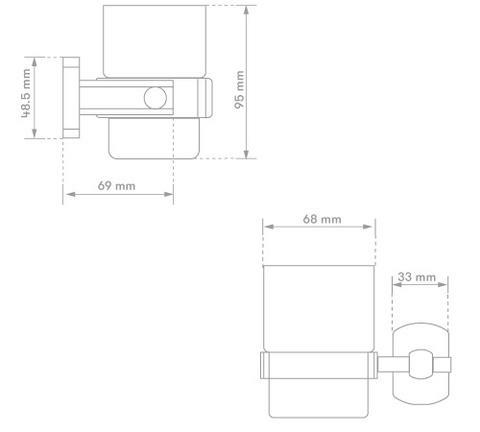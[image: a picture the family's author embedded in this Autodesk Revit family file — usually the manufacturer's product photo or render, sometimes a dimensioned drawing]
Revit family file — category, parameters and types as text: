
# Revit family: BL-2502-11 GANCHO CONTEMPRA
name_source: partatom
category: Plumbing Fixtures
revit_build: Autodesk Revit 2018 (Build: 20170223_1515(x64)
units: mm (PartAtom-declared; Revit-internal decimal feet)

## family parameters
Cut with Voids When Loaded = No
Host = Face
OmniClass Number = 23.31.11.00
Part Type = Normal
Room Calculation Point = No
Round Connector Dimension = Use Diameter
Shared = No

## types (1)
- BL-2502-11
    Alto = 70 mm  [stored 0.229659 ft]
    CW Connection = Yes
    Default Elevation = 0 mm  [stored 0 ft]
    Description = Gancho
    Diametro base = 50 mm  [stored 0.164042 ft]
    HW Connection = Yes
    Link Ficha Tecnica = http://infotecnica.gricol.com
    Manufacturer = Gricol
    Model = BL-2502-11
    Plastico ABS cromado = Plastico - ABS Cromado
    Product Name = GANCHO CONTEMPRA
    Type Image = GANCHO CONTEMPRA.jpg
    URL = https://www.gricol.com
    Vent Connection = No
    Waste Connection = No

note: [stored X ft] marks values corroborated as IEEE doubles in the binary element streams (Revit-internal decimal feet)

## geometry (parser evidence)
native form markers: Blend x2, Sweep x5
no freeform markers — native parametric forms only
